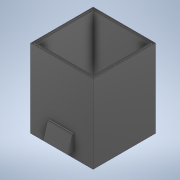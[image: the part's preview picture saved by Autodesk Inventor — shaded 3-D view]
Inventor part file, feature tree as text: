
AUTODESK INVENTOR PART (.ipt)
format: ipt  version: 2020 (Build 240168000, 168)  size: 208,896 bytes
history: native  units: mm
features: extrude x7, sketch x7, fillet x2, chamfer x1
ambient origin geometry x8: Origin, YZ Plane, XZ Plane, XY Plane, X Axis, Y Axis, Z Axis, Center Point
bodies: Volumenkörper1 (feature_tree)
feature tree (17):
  extrude  "Extrusion1"  Depth=200.0mm
  extrude  "Extrusion2"  Depth=100.0mm
  extrude  "Extrusion3"  Depth=10.0mm
  fillet  "Rundung1"  Radius=10.0mm
  extrude  "Extrusion4"  Depth=10.0mm
  extrude  "Extrusion5"  Depth=2.0mm
  extrude  "Extrusion6"  Depth=2.0mm
  extrude  "Extrusion7"  Depth=2.0mm
  fillet  "Rundung2"  Radius=2.0mm
  chamfer  "Fase1"  Distance=2.0mm
  sketch  "Skizze1"  dims[d0=200.0mm d1=200.0mm]
  sketch  "Skizze2"  dims[d2=100.0mm d3=100.0mm]
  sketch  "Skizze3"  dims[d4=200.0mm d5=0.0mm d6=10.0mm d7=10.0mm]
  sketch  "Skizze5"  dims[d8=10.0mm d9=10.0mm]
  sketch  "Skizze6"  dims[d10=190.0mm d11=0.0mm d12=2.0mm]
  sketch  "Skizze7"  dims[d13=2.0mm d14=2.0mm]
  sketch  "Skizze9"  dims[d15=2.0mm d16=2.0mm d17=2.0mm d18=2.0mm d19=2.0mm d20=5.0mm d21=0.0mm d22=0.5mm d24=10.0mm d25=10.0mm d26=95.0mm d27=95.0mm d28=7.0mm d29=0.0mm d30=10.0mm d31=10.0mm d32=10.0mm d33=10.0mm d34=50.0mm d35=0.0mm d36=50.0mm d37=80.0mm d38=20.0mm d39=60.0mm d40=20.0mm d41=0.0mm d45=5.0mm d46=200.0mm d47=0.0mm d48=2.0mm d49=1.0mm d50=2.0mm d51=45.0deg]
